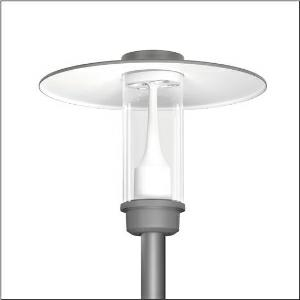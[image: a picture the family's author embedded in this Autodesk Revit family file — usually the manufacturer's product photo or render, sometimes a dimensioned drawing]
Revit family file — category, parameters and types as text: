
# Revit family: litepole_2_iq___p1_0a_5xa5425bf14h_a5ac
name_source: partatom
category: Lighting Fixtures
units: mm (PartAtom-declared; Revit-internal decimal feet)

## family parameters
Cut with Voids When Loaded = No
Host = Face
Light Source = No
Part Type = Normal
Room Calculation Point = No
Round Connector Dimension = Use Diameter
Shared = No

## types (1)
- --- (1 x LED, 1520 lm, 12.9 W, 2200K)
    Apparent Load = 13 VA
    CIE Flux Codes = 33 62 89 96 100
    Color Rendering = 70
    Color Temperature = 2200K
    Default Elevation = 1800 mm
    Description = Litepole 2 iQ, mast luminaire, Module 540 iQ-SR, primary light control with 3 zone facetted reflector, of plastic, silver coated, highly specular, structured, primary optical cover: cover, of PMMA, transparent, light distribution: P1.0a, light emission: direct distribution, primary light characteristic: strongly asymmetric, installation type: post-top, LED, High Power LED, rated luminous flux: 1.520lm, luminous efficacy: 118lm/W, light colour: 722, colour temperature: 2200K, control gear: iQ Street-Remote, control: pre-setting: logarithmic dimming characteristic, Street-Remote, Auto-Match, Temp-Guard, Lumen-Switch, Night-Set, Smart-Wire, Light-Fading, Desk-Remote (wireless, voltage-free reading and setting of iQ features in the workshop via application-optimized NFC function/RFID function), optimised constant luminous flux control (CLO 2.0), with terminal, 6-pole, max. 2.5mm², mains connection: 230..240V, AC, 50/60Hz, start of lifetime: 13W, end of service life: 13W, reduction: 6W, luminaire housing, upper part, of aluminium, coated, Siteco® metallic grey (DB 702S), diameter: 750mm, height: 590mm, spigot size: d x l = 76 x 70mm (post-top) | with reducer (optional accessory) 60 x 70mm, mounting height: 3..5m, post-top mast mounting element, of diecast aluminium, coated, Siteco® metallic grey (DB 702S), Module 540 iQ-SR, traffic white (RAL 9016), equipment: standard, protection rating (complete): IP65, insulation class (complete): insulation class II (safety insulation), certification: CE, ENEC, VDE, packaging unit: 1 piece

Light Distribution: P1.0a
    Height = 590 mm
    Lamp = 1 x LED
    Lamp Light Flux = 1520 lm
    Lamp Power = 12.9 W
    Lamp count = 1
    Length = 750 mm
    Luminous efficacy = 118 lm/W
    Manufacturer = Siteco
    ModVariant = No
    Model = 5XA5425BF14H
    Number of Poles = 1
    OnlyDefault = Yes
    Power Factor = 1
    Product Name = Litepole 2 iQ | P1.0a
    Product group = mast luminaire | pylon top
    ProductGroupID = 6100
    Protection Class = Protection class II
    Protection Degree = IP 65
    RLX_Detail_Level = 1
    RLX_Emergency_Light_Flux = 0 lm
    RLX_Emergency_Type = 0
    RLX_Emergency_Type_DB = No
    RlxData = <blob elided: 55821 chars, md5=1ba409cb>
    Socket = socket
    Standby Power = 0 W
    System Light Flux = 1520 lm
    System Power = 13 W
    Type Comments = factory setting: luminous flux: 100 % | dim-lin: 254 | 516 mA
    Type Image = l_1006518.jpg
    URL = http://relux.com
    VarID = @adj_213845
    Voltage = 0 V
    Weight = 0.00 kg
    Width = 0 mm  [stored 0 ft]

note: [stored X ft] marks values corroborated as IEEE doubles in the binary element streams (Revit-internal decimal feet)

## geometry (parser evidence)
native form markers: Blend x4, Sweep x13
no freeform markers — native parametric forms only
